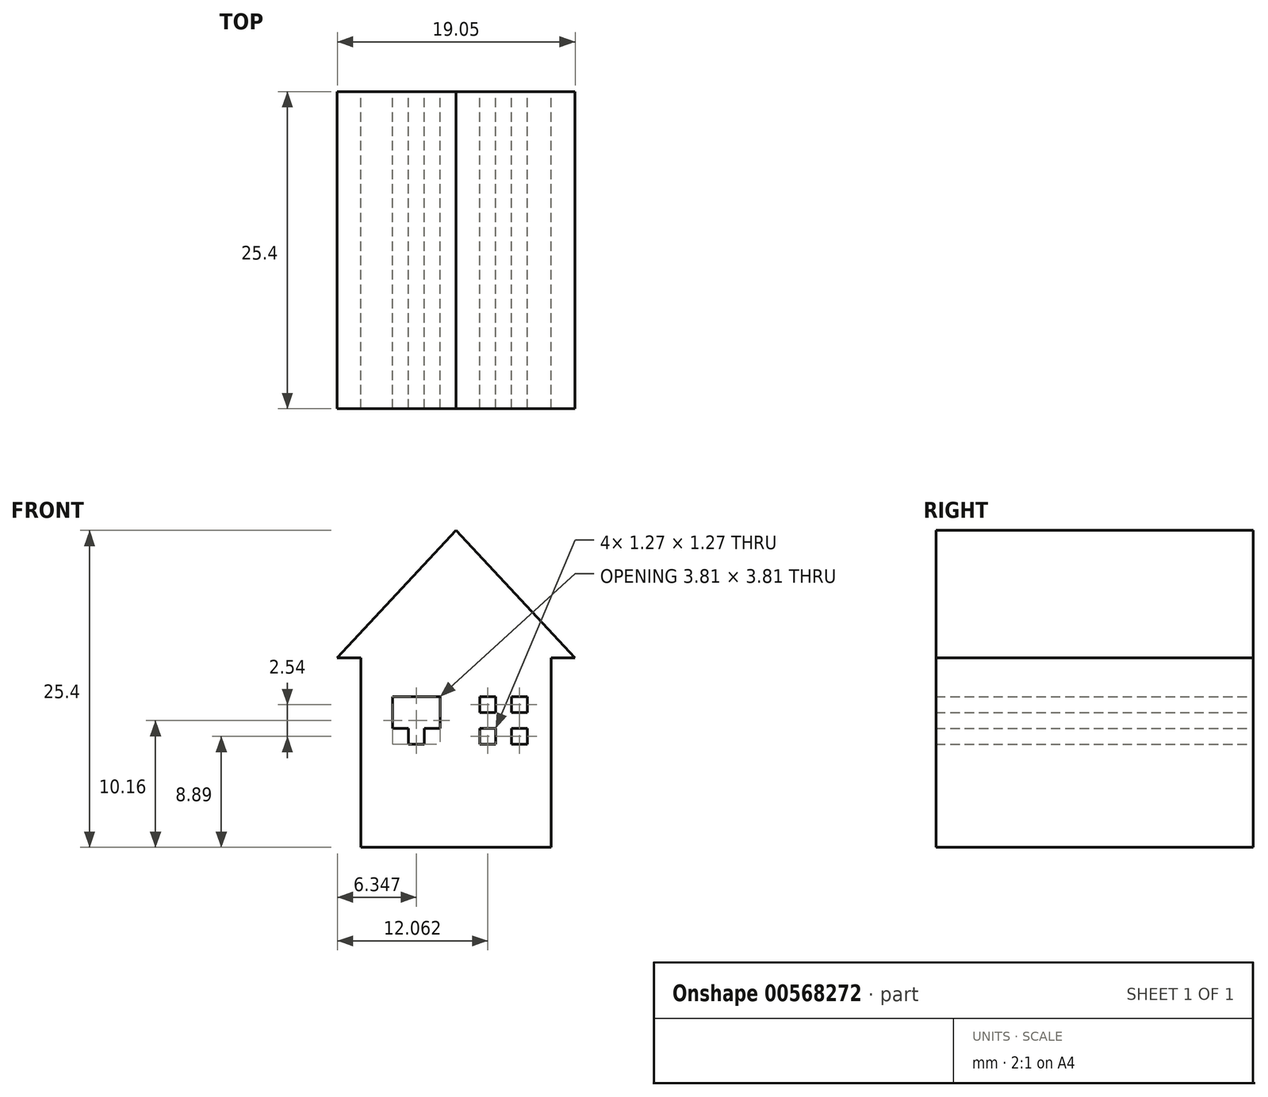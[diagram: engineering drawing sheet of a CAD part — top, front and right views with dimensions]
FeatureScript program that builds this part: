
annotation { "Feature Type Name" : "Feature", "Feature Type Description" : "" }
export const myFeature = defineFeature(function(context is Context, id is Id, definition is map)
    precondition{}
    {
        {
            var Q0;
            Q0=qCreatedBy(makeId("Front.planeOp"),FACE);
            var sketch = newSketch(context, id + "F0", { "sketchPlane" : qUnion([Q0])});
            skLineSegment(sketch, "E0", {"start": v(0, 0) * mm, "end": v(-25.4, 0) * mm});
            skLineSegment(sketch, "E1", {"start": v(-25.4, 0) * mm, "end": v(-25.4, 25.4) * mm});
            skLineSegment(sketch, "E2", {"start": v(-25.4, 25.4) * mm, "end": v(0, 25.4) * mm});
            skLineSegment(sketch, "E3", {"start": v(0, 25.4) * mm, "end": v(0, 0) * mm});
            skSolve(sketch);
        }
        {
            var Q0;
            Q0=makeQuery(id+"F0.imprint","IMPRINT",FACE,{"disambiguationData":[TD([[makeQuery(id+"F0.imprint","IMPRINT",EDGE,{"derivedFrom":sQuery(id+"F0.wireOp",EDGE,"E0")}),-1.0]])]});
            extrude(context, id + "F1", {"entities" : qUnion([Q0]), "depth" : 25.4 * mm, "offsetDistance" : 25.4 * mm});
        }
        {
            var Q0;
            Q0=makeQuery(id+"F0.imprint","IMPRINT",FACE,{"disambiguationData":[TD([[makeQuery(id+"F0.imprint","IMPRINT",EDGE,{"derivedFrom":sQuery(id+"F0.wireOp",EDGE,"E0")}),-1.0]])]});
            var sketch = newSketch(context, id + "F2", { "sketchPlane" : qUnion([Q0])});
            skLineSegment(sketch, "E4", {"start": v(-21.14, 0) * mm, "end": v(-21.14, 15.18) * mm});
            skLineSegment(sketch, "E5", {"start": v(-21.14, 15.18) * mm, "end": v(-5.9, 15.18) * mm});
            skLineSegment(sketch, "E6", {"start": v(-5.9, 15.18) * mm, "end": v(-5.9, 0) * mm});
            skLineSegment(sketch, "E7", {"start": v(-21.14, 15.18) * mm, "end": v(-23.04, 15.18) * mm});
            skLineSegment(sketch, "E8", {"start": v(-23.04, 15.18) * mm, "end": v(-13.52, 25.4) * mm});
            skLineSegment(sketch, "E9", {"start": v(-13.52, 25.4) * mm, "end": v(-4, 15.18) * mm});
            skLineSegment(sketch, "E10", {"start": v(-4, 15.18) * mm, "end": v(-5.9, 15.18) * mm});
            skLineSegment(sketch, "E11", {"start": v(-15.73, 0) * mm, "end": v(-15.73, 5.08) * mm});
            skLineSegment(sketch, "E12", {"start": v(-15.73, 5.08) * mm, "end": v(-11.29, 5.08) * mm});
            skLineSegment(sketch, "E13", {"start": v(-11.29, 5.08) * mm, "end": v(-11.29, 0) * mm});
            skLineSegment(sketch, "E14", {"start": v(-18.6, 12.07) * mm, "end": v(-18.6, 8.26) * mm});
            skLineSegment(sketch, "E15", {"start": v(-18.6, 8.26) * mm, "end": v(-14.79, 8.26) * mm});
            skLineSegment(sketch, "E16", {"start": v(-14.79, 8.25) * mm, "end": v(-14.79, 12.07) * mm});
            skLineSegment(sketch, "E17", {"start": v(-14.79, 12.07) * mm, "end": v(-18.6, 12.07) * mm});
            skLineSegment(sketch, "E18", {"start": v(-16.7, 8.26) * mm, "end": v(-18.6, 8.26) * mm});
            skLineSegment(sketch, "E19", {"start": v(-11.61, 8.26) * mm, "end": v(-7.8, 8.26) * mm});
            skLineSegment(sketch, "E20", {"start": v(-7.8, 8.26) * mm, "end": v(-7.8, 12.07) * mm});
            skLineSegment(sketch, "E21", {"start": v(-7.8, 12.07) * mm, "end": v(-11.61, 12.07) * mm});
            skLineSegment(sketch, "E22", {"start": v(-11.61, 12.07) * mm, "end": v(-11.61, 8.26) * mm});
            skLineSegment(sketch, "E23", {"start": v(-9.7, 12.07) * mm, "end": v(-11.61, 12.07) * mm});
            skLineSegment(sketch, "E24", {"start": v(-7.8, 10.8) * mm, "end": v(-9.07, 10.8) * mm});
            skLineSegment(sketch, "E25", {"start": v(-11.61, 10.8) * mm, "end": v(-11.61, 9.52) * mm});
            skLineSegment(sketch, "E26", {"start": v(-11.61, 9.52) * mm, "end": v(-10.34, 9.52) * mm});
            skLineSegment(sketch, "E27", {"start": v(-10.34, 12.07) * mm, "end": v(-10.34, 10.8) * mm});
            skLineSegment(sketch, "E28", {"start": v(-10.34, 8.26) * mm, "end": v(-9.07, 8.26) * mm});
            skLineSegment(sketch, "E29", {"start": v(-9.07, 8.26) * mm, "end": v(-9.07, 9.52) * mm});
            skPoint(sketch, "E30.start.orphan", {"position": v(-9.7, 8.26) * mm});
            skPoint(sketch, "E31.orphan", {"position": v(-7.8, 10.16) * mm});
            skPoint(sketch, "E32.start.orphan", {"position": v(-11.74, 10.16) * mm});
            skPoint(sketch, "E33.orphan", {"position": v(-16.7, 12.06) * mm});
            skPoint(sketch, "E34.end.orphan", {"position": v(-14.79, 10.16) * mm});
            skPoint(sketch, "E34.start.orphan", {"position": v(-18.6, 10.16) * mm});
            skLineSegment(sketch, "E35", {"start": v(-17.33, 12.07) * mm, "end": v(-17.33, 10.8) * mm});
            skLineSegment(sketch, "E36", {"start": v(-17.33, 8.26) * mm, "end": v(-16.06, 8.26) * mm});
            skLineSegment(sketch, "E37", {"start": v(-16.06, 8.26) * mm, "end": v(-16.06, 9.53) * mm});
            skLineSegment(sketch, "E38", {"start": v(-16.06, 12.06) * mm, "end": v(-18.6, 12.06) * mm});
            skLineSegment(sketch, "E39", {"start": v(-18.6, 10.8) * mm, "end": v(-17.33, 10.8) * mm});
            skLineSegment(sketch, "E40", {"start": v(-14.79, 10.8) * mm, "end": v(-14.79, 9.53) * mm});
            skLineSegment(sketch, "E41", {"start": v(-14.79, 9.53) * mm, "end": v(-16.06, 9.53) * mm});
            skLineSegment(sketch, "E42.trimOffspring", {"start": v(-10.34, 10.8) * mm, "end": v(-11.61, 10.8) * mm});
            skLineSegment(sketch, "E43.trimOffspring", {"start": v(-9.07, 10.8) * mm, "end": v(-9.07, 12.07) * mm});
            skLineSegment(sketch, "E44.trimOffspring", {"start": v(-9.07, 9.52) * mm, "end": v(-7.8, 9.52) * mm});
            skLineSegment(sketch, "E45.trimOffspring", {"start": v(-10.34, 9.52) * mm, "end": v(-10.34, 8.26) * mm});
            skLineSegment(sketch, "E46.trimOffspring", {"start": v(-17.33, 9.53) * mm, "end": v(-17.33, 8.26) * mm});
            skLineSegment(sketch, "E47.trimOffspring", {"start": v(-16.06, 10.8) * mm, "end": v(-16.06, 12.07) * mm});
            skLineSegment(sketch, "E48.trimOffspring", {"start": v(-16.06, 10.8) * mm, "end": v(-14.79, 10.8) * mm});
            skLineSegment(sketch, "E49.trimOffspring", {"start": v(-17.33, 9.53) * mm, "end": v(-18.6, 9.53) * mm});
            skLineSegment(sketch, "E50.bottom", {"start": v(0, 0) * mm, "end": v(-25.4, 0) * mm});
            skLineSegment(sketch, "E50.top", {"start": v(0, 25.4) * mm, "end": v(-25.4, 25.4) * mm});
            skLineSegment(sketch, "E50.left", {"start": v(0, 0) * mm, "end": v(0, 25.4) * mm});
            skLineSegment(sketch, "E50.right", {"start": v(-25.4, 0) * mm, "end": v(-25.4, 25.4) * mm});
            skLineSegment(sketch, "E51.bottom", {"start": v(-11.42, 0) * mm, "end": v(-15.58, 0) * mm});
            skLineSegment(sketch, "E51.top", {"start": v(-11.42, 4.93) * mm, "end": v(-15.58, 4.93) * mm});
            skLineSegment(sketch, "E51.left", {"start": v(-11.42, 0) * mm, "end": v(-11.42, 4.93) * mm});
            skLineSegment(sketch, "E51.right", {"start": v(-15.58, 0) * mm, "end": v(-15.58, 4.93) * mm});
            skSolve(sketch);
        }
        {
            var Q0;
            {var subQ3=sQuery(id+"F2.wireOp",EDGE,"E6");Q0=makeQuery(id+"F2.imprint","IMPRINT",FACE,{"disambiguationData":[TD([[makeQuery(id+"F2.imprint","IMPRINT",EDGE,{"derivedFrom":subQ3}),1.0]])]});}
            var Q1;
            {var subQ2=sQuery(id+"F2.wireOp",EDGE,"E4");Q1=makeQuery(id+"F2.imprint","IMPRINT",FACE,{"disambiguationData":[TD([[makeQuery(id+"F2.imprint","IMPRINT",EDGE,{"derivedFrom":subQ2}),1.0]])]});}
            extrude(context, id + "F3", {"entities" : qUnion([Q0, Q1]), "operationType" : NewBodyOperationType.REMOVE, "depth" : 25.4 * mm, "offsetDistance" : 25.4 * mm});
        }
        {
            var Q0;
            {var subQ0=sQuery(id+"F2.wireOp",EDGE,"E17");Q0=makeQuery(id+"F2.imprint","IMPRINT",FACE,{"disambiguationData":[TD([[makeQuery(id+"F2.imprint","IMPRINT",EDGE,{"derivedFrom":subQ0}),1.0]])]});}
            var Q1;
            {var subQ4=sQuery(id+"F2.wireOp",EDGE,"E35");Q1=makeQuery(id+"F2.imprint","IMPRINT",FACE,{"disambiguationData":[TD([[makeQuery(id+"F2.imprint","IMPRINT",EDGE,{"derivedFrom":subQ4}),-1.0]])]});}
            var Q2;
            {var subQ0=sQuery(id+"F2.wireOp",EDGE,"E18");Q2=makeQuery(id+"F2.imprint","IMPRINT",FACE,{"disambiguationData":[TD([[makeQuery(id+"F2.imprint","IMPRINT",EDGE,{"derivedFrom":subQ0}),-1.0]])]});}
            var Q3;
            {var subQ0=sQuery(id+"F2.wireOp",EDGE,"E15");Q3=makeQuery(id+"F2.imprint","IMPRINT",FACE,{"disambiguationData":[TD([[makeQuery(id+"F2.imprint","IMPRINT",EDGE,{"derivedFrom":subQ0}),1.0]])]});}
            var Q4;
            {var subQ4=sQuery(id+"F2.wireOp",EDGE,"E26");Q4=makeQuery(id+"F2.imprint","IMPRINT",FACE,{"disambiguationData":[TD([[makeQuery(id+"F2.imprint","IMPRINT",EDGE,{"derivedFrom":subQ4}),-1.0]])]});}
            var Q5;
            {var subQ3=sQuery(id+"F2.wireOp",EDGE,"E29");Q5=makeQuery(id+"F2.imprint","IMPRINT",FACE,{"disambiguationData":[TD([[makeQuery(id+"F2.imprint","IMPRINT",EDGE,{"derivedFrom":subQ3}),-1.0]])]});}
            var Q6;
            {var subQ3=sQuery(id+"F2.wireOp",EDGE,"E24");Q6=makeQuery(id+"F2.imprint","IMPRINT",FACE,{"disambiguationData":[TD([[makeQuery(id+"F2.imprint","IMPRINT",EDGE,{"derivedFrom":subQ3}),-1.0]])]});}
            var Q7;
            {var subQ4=sQuery(id+"F2.wireOp",EDGE,"E27");Q7=makeQuery(id+"F2.imprint","IMPRINT",FACE,{"disambiguationData":[TD([[makeQuery(id+"F2.imprint","IMPRINT",EDGE,{"derivedFrom":subQ4}),-1.0]])]});}
            extrude(context, id + "F4", {"entities" : qUnion([Q0, Q1, Q2, Q3, Q4, Q5, Q6, Q7]), "operationType" : NewBodyOperationType.REMOVE, "depth" : 25.4 * mm, "offsetDistance" : 25.4 * mm});
        }
        {
            var Q0;
            Q0=makeQuery(id+"F2.imprint","IMPRINT",FACE,{"disambiguationData":[TD([[makeQuery(id+"F2.imprint","IMPRINT",EDGE,{"derivedFrom":sQuery(id+"F2.wireOp",EDGE,"E5")}),1.0]])]});
            var sketch = newSketch(context, id + "F5", { "sketchPlane" : qUnion([Q0])});
            skCircle(sketch, "E52", {"center": v(-13.46, 21.53) * mm, "radius": 1.59 * mm});
            skSolve(sketch);
        }
        {
            var Q0;
            Q0=sQuery(id+"F5.wireOp",EDGE,"E52");
            extrude(context, id + "F6", {"bodyType" : ToolBodyType.SURFACE, "surfaceEntities" : qUnion([Q0]), "depth" : 25.4 * mm, "offsetDistance" : 25.4 * mm});
        }
    });
